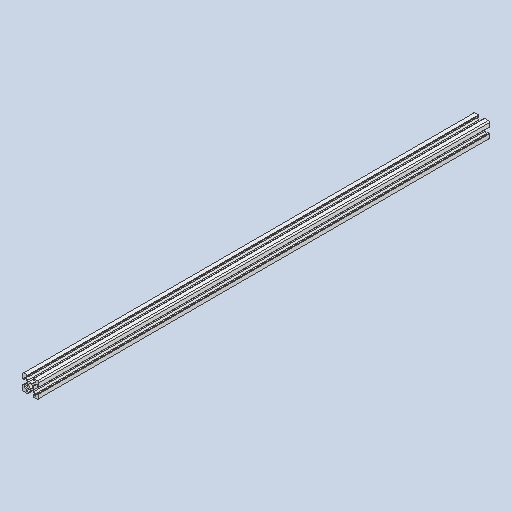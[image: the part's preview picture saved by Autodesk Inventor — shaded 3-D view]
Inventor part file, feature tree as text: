
AUTODESK INVENTOR PART (.ipt)
format: ipt  version: 2023 (Build 270158000, 158)  size: 258,048 bytes
history: native  units: mm
features: extrude x1, sketch x1, projected_geometry x1
ambient origin geometry x8: Origin, YZ Plane, XZ Plane, XY Plane, X Axis, Y Axis, Z Axis, Center Point
bodies: Solid1 (feature_tree), Body1 (feature_tree)
feature tree (3):
  extrude  "Extrusion1"  [1 undecoded]
  sketch  "Sketch1"  dims[d0=460.0mm d1=0.0mm]
  projected_geometry  "Projected Loop1"
note: 1 required parameter value undecoded (feature->parameter linkage not recoverable at this tier; creation-order binding heuristic only, values carry confidence <= 0.55)
